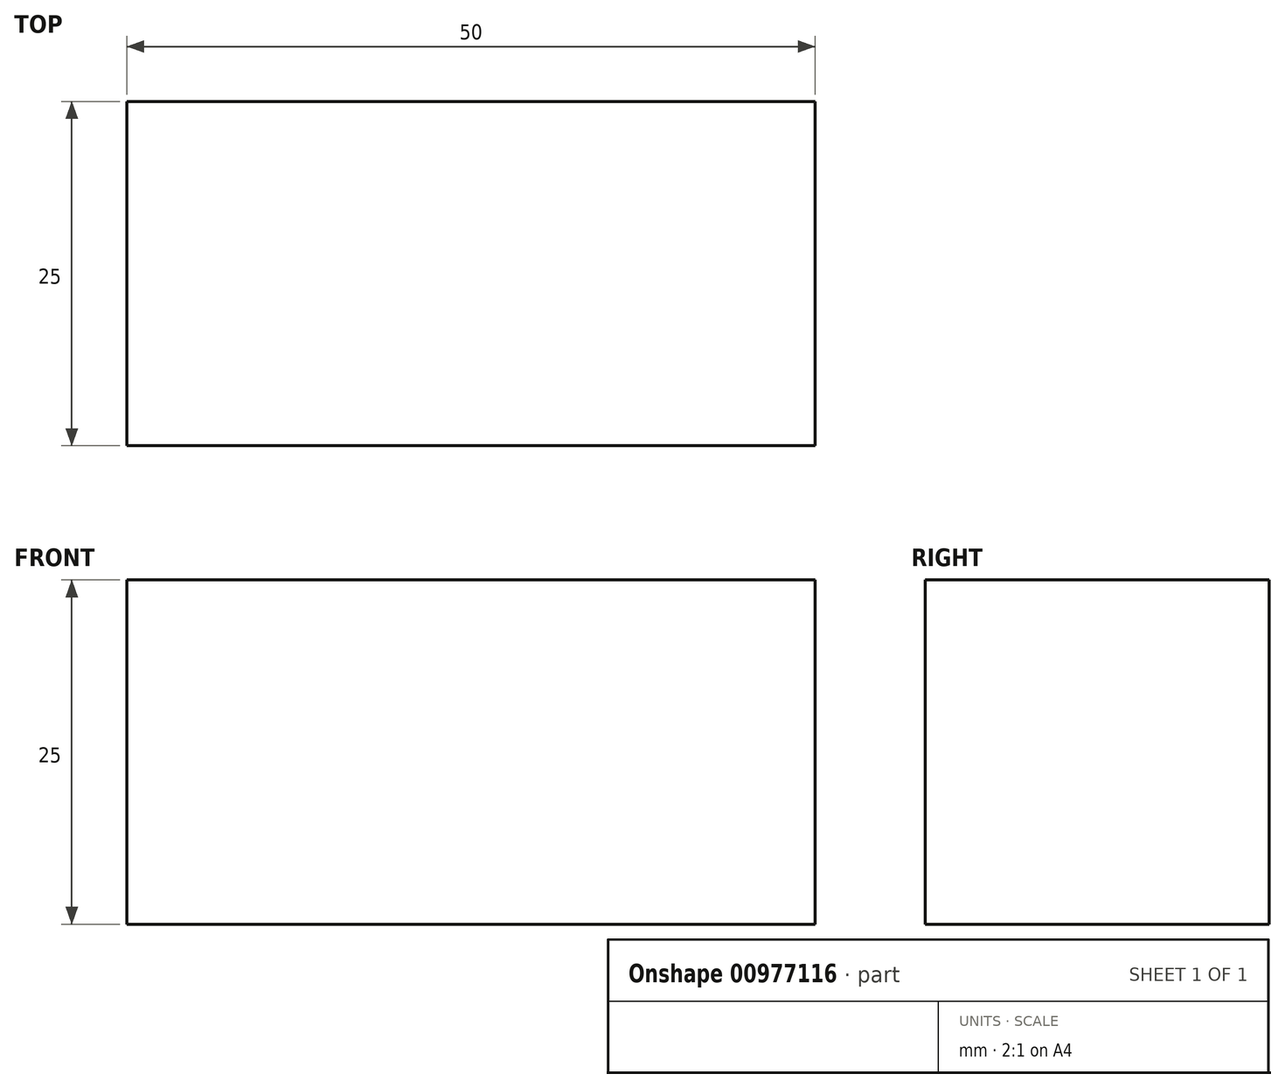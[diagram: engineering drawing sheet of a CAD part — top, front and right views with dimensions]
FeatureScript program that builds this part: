
annotation { "Feature Type Name" : "Feature", "Feature Type Description" : "" }
export const myFeature = defineFeature(function(context is Context, id is Id, definition is map)
    precondition{}
    {
        {
            var Q0;
            Q0=qCreatedBy(makeId("Top.planeOp"),FACE);
            var sketch = newSketch(context, id + "F0", { "sketchPlane" : qUnion([Q0])});
            skLineSegment(sketch, "E0.bottom", {"start": v(25, 12.5) * mm, "end": v(-25, 12.5) * mm});
            skLineSegment(sketch, "E0.top", {"start": v(25, -12.5) * mm, "end": v(-25, -12.5) * mm});
            skLineSegment(sketch, "E0.left", {"start": v(25, 12.5) * mm, "end": v(25, -12.5) * mm});
            skLineSegment(sketch, "E0.right", {"start": v(-25, 12.5) * mm, "end": v(-25, -12.5) * mm});
            skPoint(sketch, "E0.middle", {"position": v(0, 0) * mm});
            skSolve(sketch);
        }
        {
            var Q0;
            Q0 = qSketchRegion(id + "F0", true);
            extrude(context, id + "F1", {"entities" : qUnion([Q0]), "depth" : 25 * mm, "offsetDistance" : 25 * mm});
        }
    });
